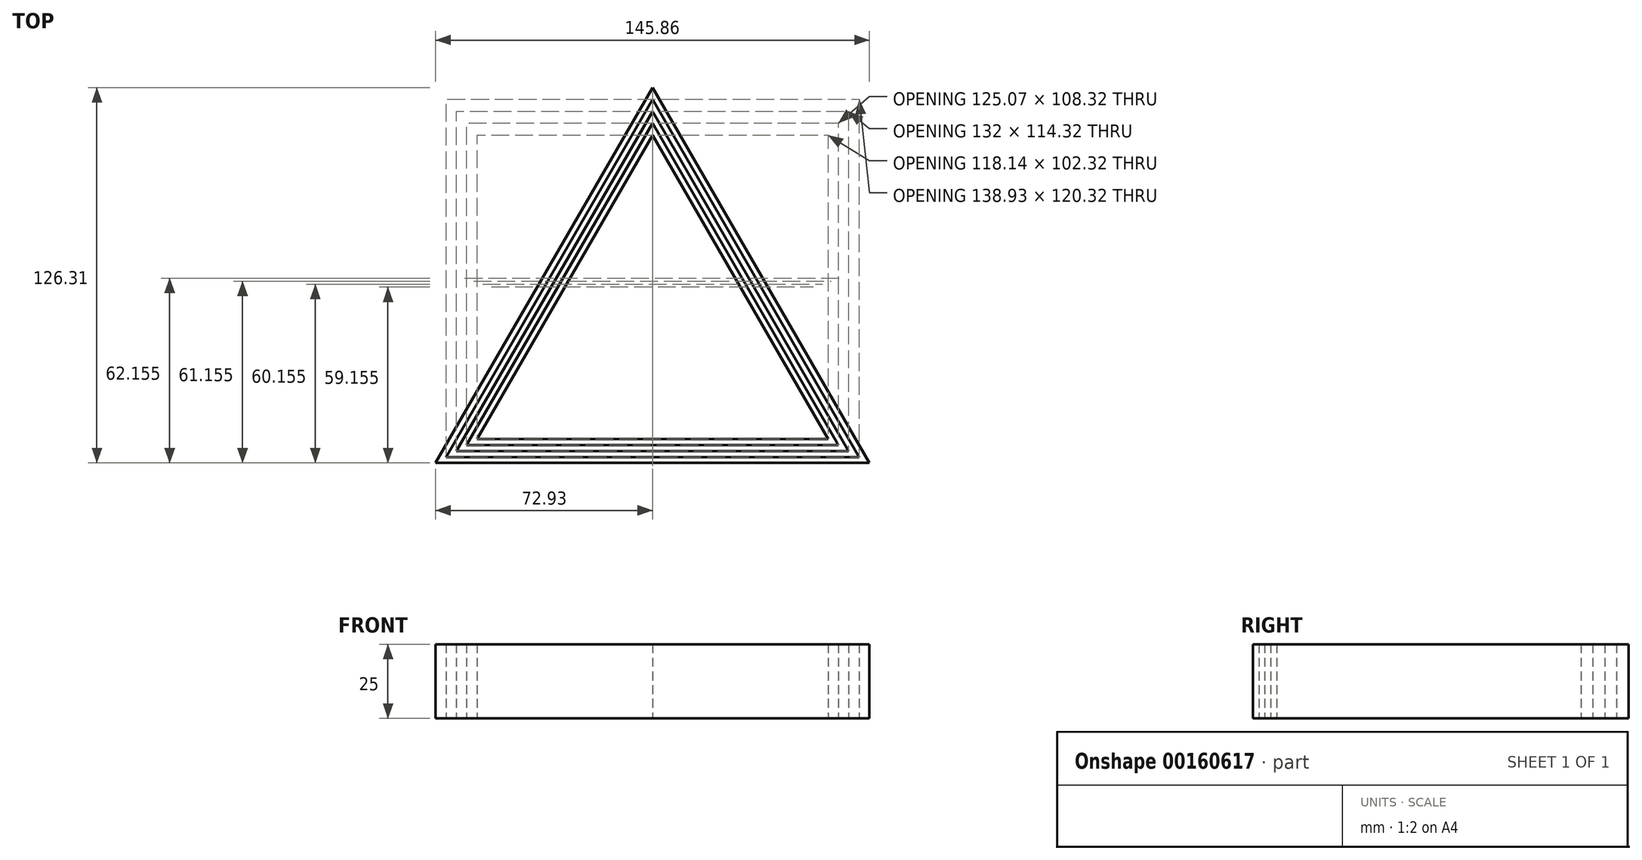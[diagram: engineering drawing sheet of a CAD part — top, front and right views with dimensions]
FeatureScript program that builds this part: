
annotation { "Feature Type Name" : "Feature", "Feature Type Description" : "" }
export const myFeature = defineFeature(function(context is Context, id is Id, definition is map)
    precondition{}
    {
        {
            var Q0;
            Q0=qCreatedBy(makeId("Top.planeOp"),FACE);
            var sketch = newSketch(context, id + "F0", { "sketchPlane" : qUnion([Q0])});
            skCircle(sketch, "E0.cCircle", {"center": v(0, 99.15) * mm, "radius": 7.13 * mm, "construction": true});
            skLineSegment(sketch, "E0.0", {"start": v(-7.13, 95.04) * mm, "end": v(-7.13, 103.27) * mm});
            skLineSegment(sketch, "E0.1", {"start": v(-7.13, 103.27) * mm, "end": v(0, 107.38) * mm});
            skLineSegment(sketch, "E0.2", {"start": v(0, 107.38) * mm, "end": v(7.12, 103.27) * mm});
            skLineSegment(sketch, "E0.3", {"start": v(7.12, 103.27) * mm, "end": v(7.12, 95.04) * mm});
            skLineSegment(sketch, "E0.4", {"start": v(7.12, 95.04) * mm, "end": v(0, 90.93) * mm});
            skLineSegment(sketch, "E0.5", {"start": v(0, 90.93) * mm, "end": v(-7.13, 95.04) * mm});
            skPoint(sketch, "E0.0.midPoint", {"position": v(-7.13, 99.15) * mm});
            skCircle(sketch, "E1.cCircle", {"center": v(8.25, 84.86) * mm, "radius": 7.13 * mm, "construction": true});
            skLineSegment(sketch, "E1.0", {"start": v(1.13, 80.75) * mm, "end": v(1.13, 88.98) * mm});
            skLineSegment(sketch, "E1.1", {"start": v(1.13, 88.98) * mm, "end": v(8.25, 93.1) * mm});
            skLineSegment(sketch, "E1.2", {"start": v(8.25, 93.1) * mm, "end": v(15.37, 88.98) * mm});
            skLineSegment(sketch, "E1.3", {"start": v(15.37, 88.98) * mm, "end": v(15.37, 80.75) * mm});
            skLineSegment(sketch, "E1.4", {"start": v(15.37, 80.75) * mm, "end": v(8.25, 76.64) * mm});
            skLineSegment(sketch, "E1.5", {"start": v(8.25, 76.64) * mm, "end": v(1.13, 80.75) * mm});
            skPoint(sketch, "E1.0.midPoint", {"position": v(1.13, 84.86) * mm});
            skLineSegment(sketch, "E2", {"start": v(-7.13, 95.04) * mm, "end": v(1.13, 80.75) * mm, "construction": true});
            skLineSegment(sketch, "E3", {"start": v(1.13, 88.98) * mm, "end": v(0, 90.93) * mm, "construction": true});
            skLineSegment(sketch, "E4", {"start": v(0, 99.15) * mm, "end": v(8.25, 84.86) * mm});
            skLineSegment(sketch, "E5", {"start": v(8.25, 84.86) * mm, "end": v(16.5, 70.57) * mm, "construction": true});
            skLineSegment(sketch, "E6", {"start": v(16.5, 70.57) * mm, "end": v(24.75, 56.28) * mm, "construction": true});
            skLineSegment(sketch, "E7", {"start": v(24.75, 56.28) * mm, "end": v(33, 42) * mm, "construction": true});
            skLineSegment(sketch, "E8", {"start": v(33, 42) * mm, "end": v(41.25, 27.7) * mm, "construction": true});
            skLineSegment(sketch, "E9", {"start": v(41.25, 27.7) * mm, "end": v(49.5, 13.42) * mm, "construction": true});
            skLineSegment(sketch, "E10", {"start": v(49.5, 13.42) * mm, "end": v(57.75, -0.87) * mm, "construction": true});
            skLineSegment(sketch, "E11", {"start": v(57.75, -0.87) * mm, "end": v(66, -15.16) * mm, "construction": true});
            skCircle(sketch, "E12.cCircle", {"center": v(0, 22.94) * mm, "radius": 38.1 * mm, "construction": true});
            skLineSegment(sketch, "E12.0", {"start": v(66, -15.16) * mm, "end": v(-66, -15.16) * mm});
            skLineSegment(sketch, "E12.1", {"start": v(-66, -15.16) * mm, "end": v(0, 99.15) * mm});
            skLineSegment(sketch, "E12.2", {"start": v(0, 99.15) * mm, "end": v(66, -15.16) * mm});
            skPoint(sketch, "E12.0.midPoint", {"position": v(0, -15.16) * mm});
            skSolve(sketch);
        }
        {
            var Q0;
            Q0=qCreatedBy(makeId("Top.planeOp"),FACE);
            var sketch = newSketch(context, id + "F1", { "sketchPlane" : qUnion([Q0])});
            skLineSegment(sketch, "E13.0", {"start": v(-66, -15.16) * mm, "end": v(0, 99.15) * mm});
            skLineSegment(sketch, "E13.1", {"start": v(66, -15.16) * mm, "end": v(-66, -15.16) * mm});
            skLineSegment(sketch, "E13.2", {"start": v(0, 99.15) * mm, "end": v(66, -15.16) * mm});
            skLineSegment(sketch, "E14.0", {"start": v(-62.54, -13.16) * mm, "end": v(0, 95.15) * mm});
            skLineSegment(sketch, "E14.1", {"start": v(62.54, -13.16) * mm, "end": v(-62.54, -13.16) * mm});
            skLineSegment(sketch, "E14.2", {"start": v(0, 95.15) * mm, "end": v(62.54, -13.16) * mm});
            skLineSegment(sketch, "E15.0", {"start": v(0, 91.15) * mm, "end": v(59.07, -11.16) * mm});
            skLineSegment(sketch, "E15.1", {"start": v(-59.07, -11.16) * mm, "end": v(0, 91.15) * mm});
            skLineSegment(sketch, "E15.2", {"start": v(59.07, -11.16) * mm, "end": v(-59.07, -11.16) * mm});
            skLineSegment(sketch, "E16.0", {"start": v(0, 103.15) * mm, "end": v(69.46, -17.16) * mm});
            skLineSegment(sketch, "E16.1", {"start": v(-69.46, -17.16) * mm, "end": v(0, 103.15) * mm});
            skLineSegment(sketch, "E16.2", {"start": v(69.46, -17.16) * mm, "end": v(-69.46, -17.16) * mm});
            skLineSegment(sketch, "E17.0", {"start": v(0, 107.15) * mm, "end": v(72.93, -19.16) * mm});
            skLineSegment(sketch, "E17.1", {"start": v(-72.93, -19.16) * mm, "end": v(0, 107.15) * mm});
            skLineSegment(sketch, "E17.2", {"start": v(72.93, -19.16) * mm, "end": v(-72.93, -19.16) * mm});
            skSolve(sketch);
        }
        {
            var Q0;
            Q0 = qSketchRegion(id + "F1", true);
            extrude(context, id + "F2", {"entities" : qUnion([Q0]), "depth" : 25 * mm});
        }
        {
            var Q0;
            Q0=makeQuery(id+"F1.imprint","IMPRINT",FACE,{"disambiguationData":[TD([[makeQuery(id+"F1.imprint","IMPRINT",EDGE,{"derivedFrom":sQuery(id+"F1.wireOp",EDGE,"E13.0")}),1.0]])]});
            extrude(context, id + "F3", {"entities" : qUnion([Q0]), "depth" : 25 * mm});
        }
        {
            var Q0;
            Q0=makeQuery(id+"F1.imprint","IMPRINT",FACE,{"disambiguationData":[TD([[makeQuery(id+"F1.imprint","IMPRINT",EDGE,{"derivedFrom":sQuery(id+"F1.wireOp",EDGE,"E14.0")}),-1.0]])]});
            extrude(context, id + "F4", {"entities" : qUnion([Q0]), "depth" : 25 * mm});
        }
        {
            var Q0;
            Q0=makeQuery(id+"F1.imprint","IMPRINT",FACE,{"disambiguationData":[TD([[makeQuery(id+"F1.imprint","IMPRINT",EDGE,{"derivedFrom":sQuery(id+"F1.wireOp",EDGE,"E13.0")}),-1.0]])]});
            extrude(context, id + "F5", {"entities" : qUnion([Q0]), "depth" : 25 * mm});
        }
    });
